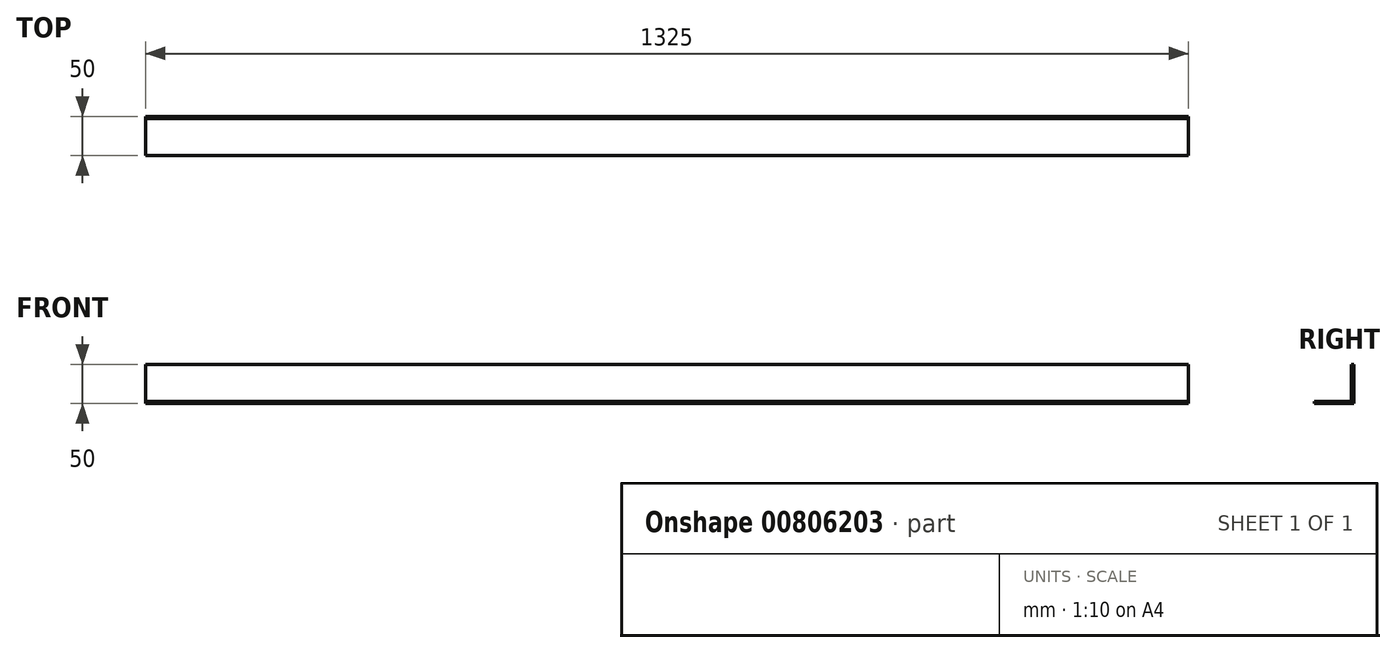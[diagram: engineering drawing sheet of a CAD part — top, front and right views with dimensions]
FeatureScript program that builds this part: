
annotation { "Feature Type Name" : "Feature", "Feature Type Description" : "" }
export const myFeature = defineFeature(function(context is Context, id is Id, definition is map)
    precondition{}
    {
        {
            var Q0;
            Q0=qCreatedBy(makeId("Right.planeOp"),FACE);
            var sketch = newSketch(context, id + "F0", { "sketchPlane" : qUnion([Q0])});
            skLineSegment(sketch, "E0", {"start": v(0, 0) * mm, "end": v(0, 50) * mm});
            skLineSegment(sketch, "E1", {"start": v(0, 0) * mm, "end": v(-50, 0) * mm});
            skLineSegment(sketch, "E2.0", {"start": v(-3, 3) * mm, "end": v(-3, 50) * mm});
            skLineSegment(sketch, "E2.1", {"start": v(-3, 3) * mm, "end": v(-50, 3) * mm});
            skLineSegment(sketch, "E3", {"start": v(0, 50) * mm, "end": v(-3, 50) * mm});
            skLineSegment(sketch, "E4", {"start": v(-50, 0) * mm, "end": v(-50, 3) * mm});
            skSolve(sketch);
        }
        {
            var Q0;
            Q0=qSketchRegion(id+"F0",true);
            extrude(context, id + "F1", {"entities" : qUnion([Q0]), "depth" : 1325 * mm, "offsetDistance" : 25 * mm});
        }
    });
